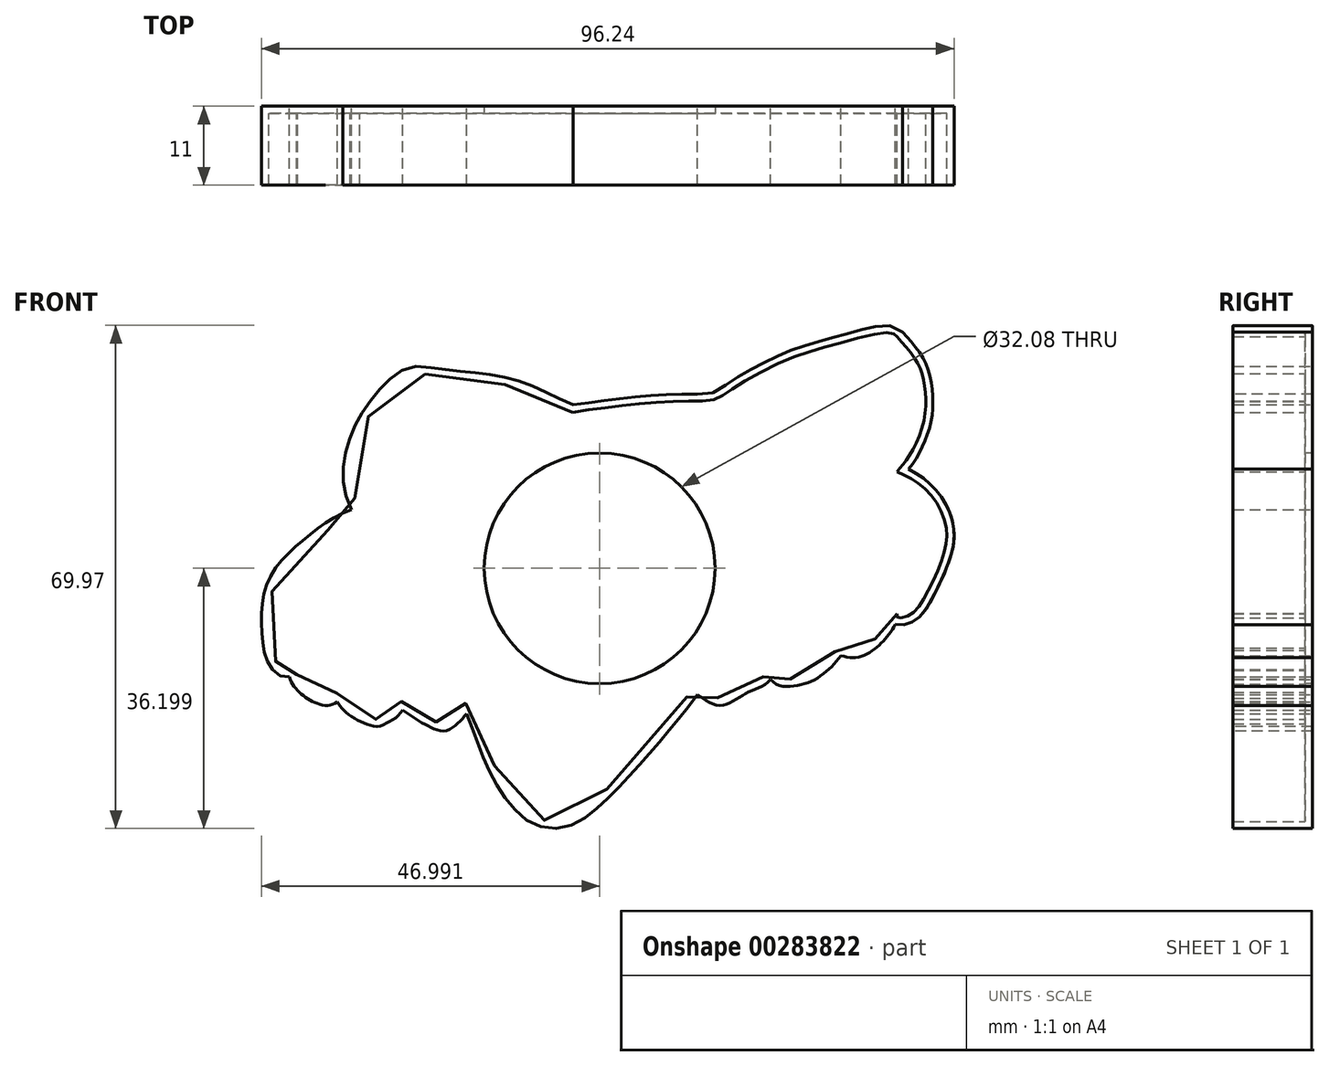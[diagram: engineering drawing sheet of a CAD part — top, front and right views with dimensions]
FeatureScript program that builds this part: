
annotation { "Feature Type Name" : "Feature", "Feature Type Description" : "" }
export const myFeature = defineFeature(function(context is Context, id is Id, definition is map)
    precondition{}
    {
        {
            var Q0;
            Q0=qCreatedBy(makeId("Front.planeOp"),FACE);
            var sketch = newSketch(context, id + "F0", { "sketchPlane" : qUnion([Q0])});
            skFitSpline(sketch, "E0", {"points": [v(5.62, 26.96) * mm, v(13.12, 27.96) * mm, v(20.78, 28.5) * mm, v(25.37, 28.72) * mm, v(28.05, 30.33) * mm, v(35.7, 34.39) * mm, v(42.37, 36.45) * mm, v(49.18, 38.03) * mm, v(50.45, 37.75) * mm, v(50.72, 37.48) * mm], "startDerivative": vector(52.2, 7.47) * mm, "endDerivative": vector(7, -8.76) * mm});
            skFitSpline(sketch, "E1", {"points": [v(50.72, 37.48) * mm, v(53.55, 33.86) * mm, v(54.55, 30.56) * mm, v(54.43, 25.65) * mm, v(52.29, 20.67) * mm, v(50.72, 18.68) * mm], "startDerivative": vector(15.33, -17.14) * mm, "endDerivative": vector(-9.62, -10.82) * mm});
            skFitSpline(sketch, "E2", {"points": [v(50.72, 18.68) * mm, v(53.66, 17.07) * mm, v(56.5, 13.93) * mm, v(57.65, 10.1) * mm, v(56.96, 6.43) * mm, v(54.54, 1.19) * mm, v(52.38, -1.3) * mm, v(50.72, -1.52) * mm, v(50.72, -1.09) * mm], "startDerivative": vector(22.7, -10.4) * mm, "endDerivative": vector(3.3, 10.75) * mm});
            skFitSpline(sketch, "E3", {"points": [v(50.72, -1.09) * mm, v(50.43, -1) * mm, v(50.31, -1.09) * mm, v(49.84, -1.38) * mm, v(49.78, -1.52) * mm, v(49.07, -2.97) * mm, v(45.98, -5.82) * mm, v(43.81, -6.1) * mm, v(42.62, -5.88) * mm, v(41.8, -6.74) * mm, v(38.83, -9.34) * mm, v(36.61, -10.04) * mm, v(34.72, -10.1) * mm, v(33.74, -9.45) * mm, v(32.99, -8.96) * mm, v(32.55, -9.29) * mm, v(31.96, -9.99) * mm, v(29.41, -11.18) * mm, v(26.54, -12.75) * mm, v(25.08, -12.48) * mm, v(23.08, -11.13) * mm, v(22.65, -10.86) * mm, v(22.37, -11.34) * mm, v(15.04, -20.41) * mm, v(6.22, -28.97) * mm, v(2.8, -29.94) * mm, v(0, -29.04) * mm, v(-4.08, -24.34) * mm, v(-7.3, -16.8) * mm, v(-8.85, -13.65) * mm, v(-9.49, -13.59) * mm, v(-9.75, -14.1) * mm, v(-11.25, -15.79) * mm, v(-12.55, -16.36) * mm, v(-14.39, -15.57) * mm, v(-14.8, -15.38) * mm, v(-17.42, -13.68) * mm, v(-18.1, -13.27) * mm, v(-18.34, -13.35) * mm, v(-19.53, -14.73) * mm, v(-20.29, -15.16) * mm, v(-21.18, -15.68) * mm, v(-21.75, -15.73) * mm, v(-25.27, -13.97) * mm, v(-26.65, -12.05) * mm, v(-26.95, -12) * mm, v(-28.22, -12.78) * mm, v(-31.42, -11.44) * mm, v(-32.7, -9.5) * mm, v(-32.61, -8.9) * mm, v(-33.22, -8.83) * mm, v(-33.8, -8.83) * mm, v(-34.48, -8.83) * mm, v(-35.77, -7.44) * mm, v(-36.47, -4.48) * mm, v(-35.91, 2.68) * mm, v(-31.54, 8.09) * mm, v(-26.13, 11.89) * mm, v(-24, 12.92) * mm, v(-24.13, 13.7) * mm, v(-25.23, 17.3) * mm, v(-23.46, 25.1) * mm, v(-17.73, 31.84) * mm, v(-15.18, 32.3) * mm, v(-11.72, 31.84) * mm, v(-2.89, 30.57) * mm, v(3.94, 27.65) * mm, v(5.62, 26.96) * mm], "startDerivative": vector(-62.6, 24.57) * mm, "endDerivative": vector(105.76, -38.61) * mm});
            skSolve(sketch);
        }
        {
            var Q0;
            Q0=makeQuery(id+"F0.imprint","IMPRINT",FACE,{"disambiguationData":[TD([[makeQuery(id+"F0.imprint","IMPRINT",EDGE,{"derivedFrom":sQuery(id+"F0.wireOp",EDGE,"E0")}),-1.0]])]});
            extrude(context, id + "F1", {"entities" : qUnion([Q0]), "depth" : 10 * mm});
        }
        {
            var Q0;
            Q0=makeQuery(id+"F1.opExtrude","CAP_FACE",FACE,{"disambiguationData":[OSD([sQuery(id+"F0.wireOp",EDGE,"E0"),sQuery(id+"F0.wireOp",EDGE,"E1"),sQuery(id+"F0.wireOp",EDGE,"E2"),sQuery(id+"F0.wireOp",EDGE,"E3")])],"isStart":false});
            shell(context, id + "F2", {"entities" : qUnion([Q0]), "thickness" : 1 * mm, "oppositeDirection" : true});
        }
        {
            var Q0;
            Q0=qCreatedBy(makeId("Front.planeOp"),FACE);
            var sketch = newSketch(context, id + "F3", { "sketchPlane" : qUnion([Q0])});
            skCircle(sketch, "E4", {"center": v(9.4, 5.26) * mm, "radius": 16.04 * mm});
            skSolve(sketch);
        }
        {
            var Q0;
            Q0=makeQuery(id+"F3.imprint","IMPRINT",FACE,{"disambiguationData":[TD([[makeQuery(id+"F3.imprint","IMPRINT",EDGE,{"derivedFrom":sQuery(id+"F3.wireOp",EDGE,"E4")}),1.0]])]});
            extrude(context, id + "F4", {"entities" : qUnion([Q0]), "operationType" : NewBodyOperationType.REMOVE, "oppositeDirection" : true, "depth" : 25.4 * mm});
        }
    });
